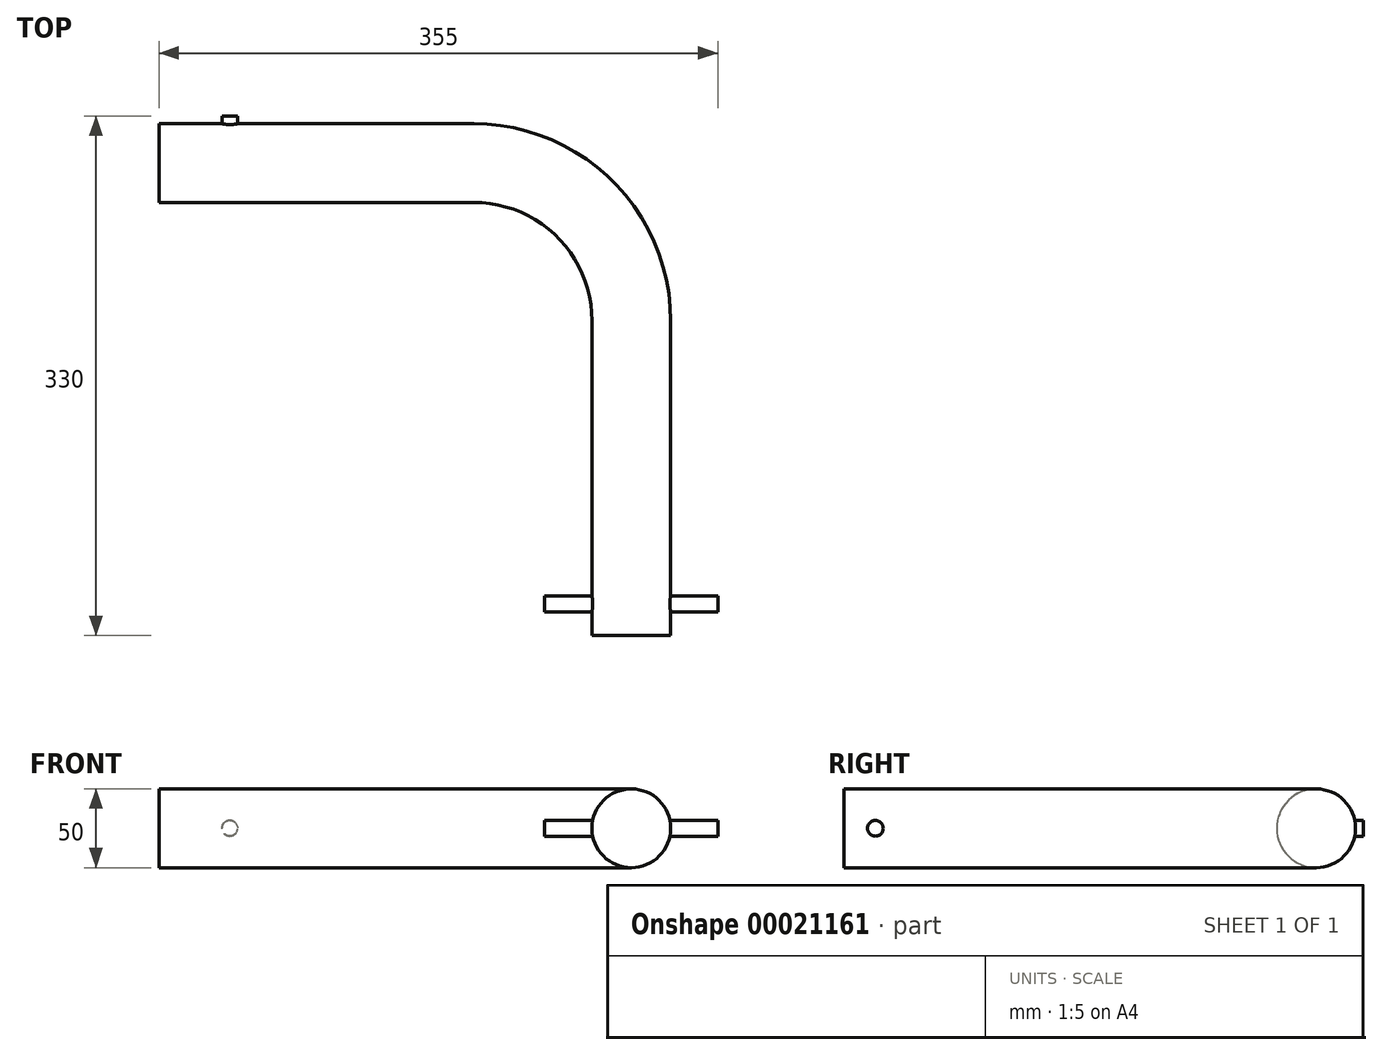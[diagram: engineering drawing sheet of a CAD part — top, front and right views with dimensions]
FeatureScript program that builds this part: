
annotation { "Feature Type Name" : "Feature", "Feature Type Description" : "" }
export const myFeature = defineFeature(function(context is Context, id is Id, definition is map)
    precondition{}
    {
        {
            var Q0;
            Q0=qCreatedBy(makeId("Top.planeOp"),FACE);
            var sketch = newSketch(context, id + "F0", { "sketchPlane" : qUnion([Q0])});
            skLineSegment(sketch, "E0", {"start": v(0, 0) * mm, "end": v(0, 200) * mm});
            skLineSegment(sketch, "E1", {"start": v(-100, 300) * mm, "end": v(-300, 300) * mm});
            skPoint(sketch, "E2.visualSharp", {"position": v(0, 300) * mm});
            skArc(sketch, "E2.filletArc", {"start": v(0, 200) * mm, "mid": v(-29.29, 270.71) * mm, "end": v(-100, 300) * mm});
            skSolve(sketch);
        }
        {
            var Q0;
            Q0=qCreatedBy(makeId("Front.planeOp"),FACE);
            var sketch = newSketch(context, id + "F1", { "sketchPlane" : qUnion([Q0])});
            skCircle(sketch, "E3", {"center": v(0, 0) * mm, "radius": 25 * mm});
            skSolve(sketch);
        }
        {
            var Q0;
            Q0=makeQuery(id+"F1.imprint","IMPRINT",FACE,{"disambiguationData":[TD([[makeQuery(id+"F1.imprint","IMPRINT",EDGE,{"derivedFrom":sQuery(id+"F1.wireOp",EDGE,"E3")}),1.0]])]});
            var Q1;
            Q1=sQuery(id+"F0.wireOp",EDGE,"E0");
            var Q2;
            Q2=sQuery(id+"F0.wireOp",EDGE,"E2.filletArc");
            var Q3;
            Q3=sQuery(id+"F0.wireOp",EDGE,"E1");
            sweep(context, id + "F2", {"profiles" : qUnion([Q0]), "path" : qUnion([Q1, Q2, Q3])});
        }
        {
            var Q0;
            Q0=qCreatedBy(makeId("Right.planeOp"),FACE);
            var sketch = newSketch(context, id + "F3", { "sketchPlane" : qUnion([Q0])});
            skCircle(sketch, "E4", {"center": v(20, 0) * mm, "radius": 5 * mm});
            skSolve(sketch);
        }
        {
            var Q0;
            Q0 = qSketchRegion(id + "F3", true);
            extrude(context, id + "F4", {"entities" : qUnion([Q0]), "operationType" : NewBodyOperationType.ADD, "endBound" : BoundingType.SYMMETRIC, "depth" : 110 * mm});
        }
        {
            var Q0;
            Q0=makeQuery(id+"F2.opSweep","CAP_FACE",FACE,{"disambiguationData":[OSD([sQuery(id+"F0.wireOp",VERTEX,"E0.start"),sQuery(id+"F1.wireOp",EDGE,"E3")])],"isStart":true});
            cPlane(context, id + "F5", {"entities" : qUnion([Q0]), "cplaneType" : CPlaneType.OFFSET, "offset" : (300 + 30) * mm, "oppositeDirection" : true, "width" : 150 * mm, "height" : 150 * mm});
        }
        {
            var Q0;
            Q0=qCreatedBy(id+"F5.planeOp",FACE);
            var sketch = newSketch(context, id + "F6", { "sketchPlane" : qUnion([Q0])});
            skCircle(sketch, "E5", {"center": v(-255, 0) * mm, "radius": 5 * mm});
            skSolve(sketch);
        }
        {
            var Q0;
            Q0=makeQuery(id+"F6.imprint","IMPRINT",FACE,{"disambiguationData":[TD([[makeQuery(id+"F6.imprint","IMPRINT",EDGE,{"derivedFrom":sQuery(id+"F6.wireOp",EDGE,"E5")}),1.0]])]});
            extrude(context, id + "F7", {"entities" : qUnion([Q0]), "operationType" : NewBodyOperationType.ADD, "endBound" : BoundingType.UP_TO_NEXT, "depth" : 25 * mm});
        }
    });
